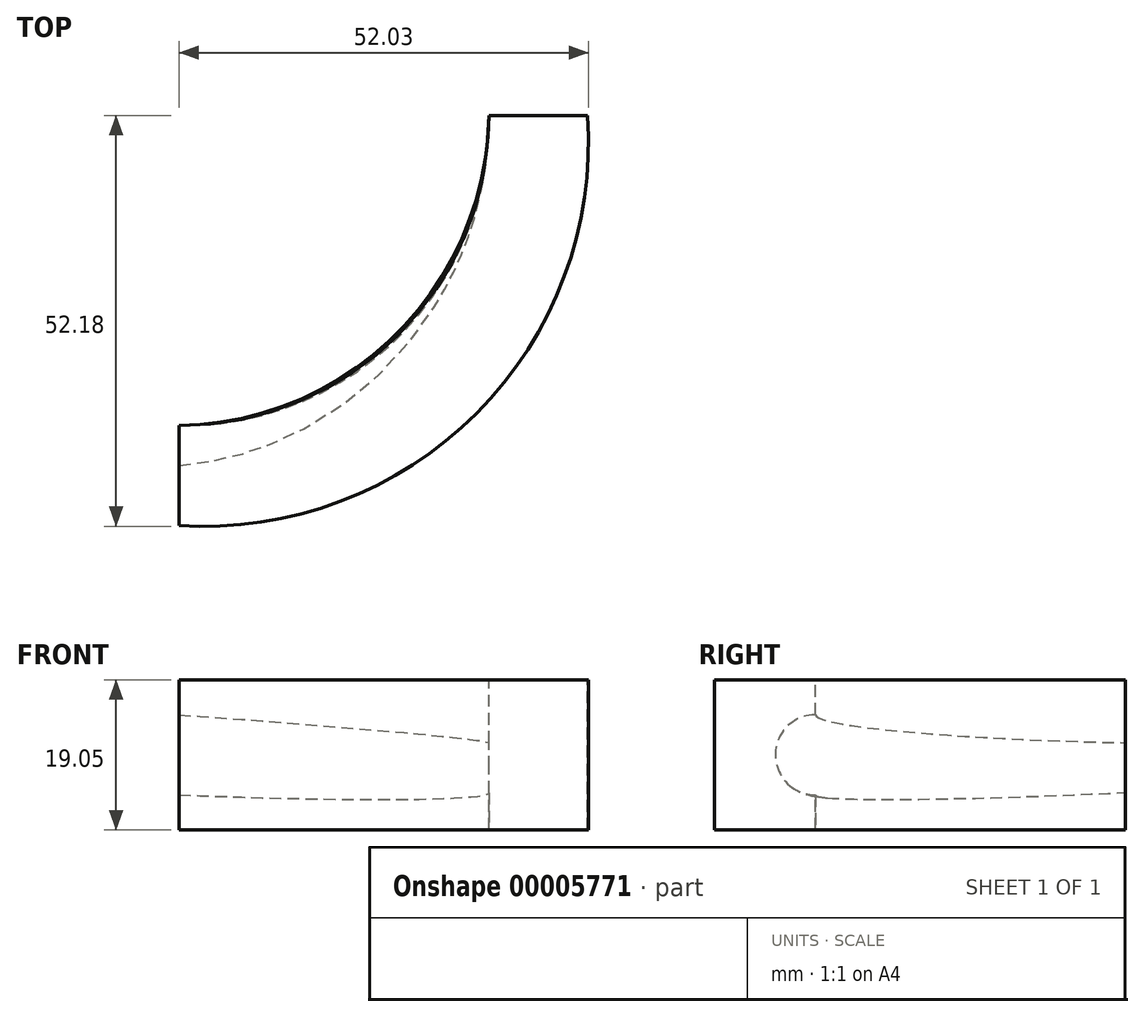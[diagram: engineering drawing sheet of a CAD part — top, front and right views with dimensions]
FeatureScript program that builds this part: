
annotation { "Feature Type Name" : "Feature", "Feature Type Description" : "" }
export const myFeature = defineFeature(function(context is Context, id is Id, definition is map)
    precondition{}
    {
        {
            var Q0;
            Q0=qCreatedBy(makeId("Top.planeOp"),FACE);
            var sketch = newSketch(context, id + "F0", { "sketchPlane" : qUnion([Q0])});
            skLineSegment(sketch, "E0", {"start": v(-39.37, 0) * mm, "end": v(39.37, 0) * mm, "construction": true});
            skLineSegment(sketch, "E1", {"start": v(0, -39.37) * mm, "end": v(0, 39.37) * mm, "construction": true});
            skArc(sketch, "E2", {"start": v(0, -39.37) * mm, "mid": v(27.84, -27.84) * mm, "end": v(39.37, 0) * mm});
            skArc(sketch, "E3", {"start": v(-39.37, 0) * mm, "mid": v(-27.84, -27.84) * mm, "end": v(0, -39.37) * mm});
            skArc(sketch, "E4", {"start": v(0, 39.37) * mm, "mid": v(-27.84, 27.84) * mm, "end": v(-39.37, 0) * mm});
            skArc(sketch, "E5", {"start": v(39.37, 0) * mm, "mid": v(27.84, 27.84) * mm, "end": v(0, 39.37) * mm});
            skSolve(sketch);
        }
        {
            var Q0;
            Q0=qCreatedBy(makeId("Front.planeOp"),FACE);
            var sketch = newSketch(context, id + "F1", { "sketchPlane" : qUnion([Q0])});
            skLineSegment(sketch, "E6", {"start": v(0, -76.2) * mm, "end": v(0, 76.2) * mm, "construction": true});
            skPoint(sketch, "E7", {"position": v(0, 13.82) * mm});
            skPoint(sketch, "E8", {"position": v(0, 6.31) * mm});
            skSolve(sketch);
        }
        {
            var Q0;
            Q0=qCreatedBy(makeId("Right.planeOp"),FACE);
            var sketch = newSketch(context, id + "F2", { "sketchPlane" : qUnion([Q0])});
            skLineSegment(sketch, "E9.0", {"start": v(-39.37, 0) * mm, "end": v(39.37, 0) * mm, "construction": true});
            skLineSegment(sketch, "E10.bottom", {"start": v(39.37, 0) * mm, "end": v(45.72, 0) * mm});
            skLineSegment(sketch, "E10.top", {"start": v(39.37, 19.05) * mm, "end": v(45.72, 19.05) * mm});
            skLineSegment(sketch, "E10.left", {"start": v(39.37, 0) * mm, "end": v(39.37, 19.05) * mm});
            skLineSegment(sketch, "E10.right", {"start": v(45.72, 0) * mm, "end": v(45.72, 19.05) * mm});
            skLineSegment(sketch, "E11.bottom", {"start": v(-39.37, 0) * mm, "end": v(-52.07, 0) * mm});
            skLineSegment(sketch, "E11.top", {"start": v(-39.37, 19.05) * mm, "end": v(-52.07, 19.05) * mm});
            skLineSegment(sketch, "E11.left", {"start": v(-39.37, 0) * mm, "end": v(-39.37, 4.45) * mm});
            skLineSegment(sketch, "E11.right", {"start": v(-52.07, 0) * mm, "end": v(-52.07, 19.05) * mm});
            skArc(sketch, "E12", {"start": v(-39.37, 14.6) * mm, "mid": v(-44.45, 9.52) * mm, "end": v(-39.37, 4.44) * mm});
            skLineSegment(sketch, "E13.trimOffspring", {"start": v(-39.37, 14.6) * mm, "end": v(-39.37, 19.05) * mm});
            skLineSegment(sketch, "E14", {"start": v(-39.37, 14.6) * mm, "end": v(-39.37, 4.45) * mm, "construction": true});
            skLineSegment(sketch, "E15", {"start": v(-39.37, 9.53) * mm, "end": v(-52.07, 9.52) * mm, "construction": true});
            skLineSegment(sketch, "E16", {"start": v(-42.33, 14.6) * mm, "end": v(-39.37, 14.6) * mm, "construction": true});
            skSolve(sketch);
        }
        {
            var Q0;
            Q0=qCreatedBy(makeId("Front.planeOp"),FACE);
            var sketch = newSketch(context, id + "F3", { "sketchPlane" : qUnion([Q0])});
            skLineSegment(sketch, "E17.bottom", {"start": v(-39.37, 0) * mm, "end": v(-53.86, 0) * mm});
            skLineSegment(sketch, "E17.top", {"start": v(-39.37, 19.05) * mm, "end": v(-53.86, 19.05) * mm});
            skLineSegment(sketch, "E17.left", {"start": v(-39.37, 0) * mm, "end": v(-39.37, 19.05) * mm});
            skLineSegment(sketch, "E17.right", {"start": v(-53.86, 0) * mm, "end": v(-53.86, 19.05) * mm});
            skLineSegment(sketch, "E18.bottom", {"start": v(39.37, 0) * mm, "end": v(51.91, 0) * mm});
            skLineSegment(sketch, "E18.top", {"start": v(39.37, 19.05) * mm, "end": v(51.91, 19.05) * mm});
            skLineSegment(sketch, "E18.left", {"start": v(39.37, 0) * mm, "end": v(39.37, 4.74) * mm});
            skLineSegment(sketch, "E18.right", {"start": v(51.91, 0) * mm, "end": v(51.91, 19.05) * mm});
            skLineSegment(sketch, "E19", {"start": v(39.37, 11.06) * mm, "end": v(39.37, 19.05) * mm});
            skLineSegment(sketch, "E20", {"start": v(39.37, 4.74) * mm, "end": v(39.37, 11.06) * mm});
            skSolve(sketch);
        }
        {
            var Q0;
            Q0=qCreatedBy(makeId("Top.planeOp"),FACE);
            var sketch = newSketch(context, id + "F4", { "sketchPlane" : qUnion([Q0])});
            skPoint(sketch, "E21.0", {"position": v(0, 45.72) * mm});
            skPoint(sketch, "E22.0", {"position": v(51.91, 0) * mm});
            skArc(sketch, "E23", {"start": v(51.91, 0) * mm, "mid": v(35.35, 33.53) * mm, "end": v(0, 45.72) * mm});
            skPoint(sketch, "E24.0", {"position": v(0, -52.07) * mm});
            skArc(sketch, "E25", {"start": v(0, -52.07) * mm, "mid": v(37.78, -37.83) * mm, "end": v(51.91, 0) * mm});
            skSolve(sketch);
        }
        {
            var Q0;
            Q0=sQuery(id+"F3.wireOp",VERTEX,"E19.end");
            var Q1;
            Q1=sQuery(id+"F2.wireOp",VERTEX,"E11.right.end");
            var Q2;
            Q2=sQuery(id+"F2.wireOp",VERTEX,"E11.top.start");
            cPlane(context, id + "F5", {"entities" : qUnion([Q0, Q1, Q2]), "cplaneType" : CPlaneType.THREE_POINT, "offset" : 152.4 * mm, "width" : 152.4 * mm, "height" : 152.4 * mm});
        }
        {
            var Q0;
            Q0=qCreatedBy(id+"F5.planeOp",FACE);
            var sketch = newSketch(context, id + "F6", { "sketchPlane" : qUnion([Q0])});
            skArc(sketch, "E26.0", {"start": v(0, -39.37) * mm, "mid": v(27.84, -27.84) * mm, "end": v(39.37, 0) * mm});
            skArc(sketch, "E27.0", {"start": v(0, -52.07) * mm, "mid": v(37.78, -37.83) * mm, "end": v(51.91, 0) * mm});
            skSolve(sketch);
        }
        {
            var Q0;
            Q0=sQuery(id+"F3.wireOp",VERTEX,"E20.end");
            var Q1;
            Q1=sQuery(id+"F2.wireOp",VERTEX,"E13.trimOffspring.start");
            var Q2;
            Q2=sQuery(id+"F1.wireOp",VERTEX,"E7");
            cPlane(context, id + "F7", {"entities" : qUnion([Q0, Q1, Q2]), "cplaneType" : CPlaneType.THREE_POINT, "offset" : 152.4 * mm, "width" : 152.4 * mm, "height" : 152.4 * mm});
        }
        {
            var Q0;
            Q0=sQuery(id+"F1.wireOp",VERTEX,"E8");
            var Q1;
            Q1=sQuery(id+"F3.wireOp",VERTEX,"E18.left.end");
            var Q2;
            Q2=sQuery(id+"F2.wireOp",VERTEX,"E12.end");
            cPlane(context, id + "F8", {"entities" : qUnion([Q0, Q1, Q2]), "cplaneType" : CPlaneType.THREE_POINT, "offset" : 152.4 * mm, "width" : 152.4 * mm, "height" : 152.4 * mm});
        }
        {
            var Q0;
            Q0=qCreatedBy(id+"F7.planeOp",FACE);
            var sketch = newSketch(context, id + "F9", { "sketchPlane" : qUnion([Q0])});
            skPoint(sketch, "E28.0", {"position": v(38.5, -0.22) * mm});
            skPoint(sketch, "E29.0", {"position": v(-0.96, -39.65) * mm});
            skFitSpline(sketch, "E30.0", {"points": [v(-12.2, 37.46) * mm, v(1000, -87.68) * mm, v(15.78, 333.33) * mm, v(-65.94, -59.9) * mm, v(333.33, 9.54) * mm, v(-38.22, 1000) * mm, v(85.02, -16.54) * mm], "construction": true});
            skArc(sketch, "E31", {"start": v(-0.96, -39.65) * mm, "mid": v(26.76, -27.93) * mm, "end": v(38.5, -0.22) * mm});
            skPoint(sketch, "E32", {"position": v(26.76, -27.93) * mm});
            skSolve(sketch);
        }
        {
            var Q0;
            Q0=qCreatedBy(id+"F8.planeOp",FACE);
            var sketch = newSketch(context, id + "F10", { "sketchPlane" : qUnion([Q0])});
            skFitSpline(sketch, "E33.0", {"points": [v(30.18, 25.29) * mm, v(1000, -20.3) * mm, v(85.52, 333.33) * mm, v(-80.65, 34.95) * mm, v(333.33, -30.18) * mm, v(-25.29, 1000) * mm, v(20.3, -85.52) * mm], "construction": true});
            skPoint(sketch, "E34.0", {"position": v(39.15, 0.22) * mm});
            skPoint(sketch, "E35.0", {"position": v(-0.25, -39.11) * mm});
            skArc(sketch, "E36", {"start": v(-0.25, -39.11) * mm, "mid": v(27.78, -27.8) * mm, "end": v(39.15, 0.22) * mm});
            skPoint(sketch, "E37", {"position": v(27.78, -27.8) * mm});
            skSolve(sketch);
        }
        {
            var Q0;
            Q0=makeQuery(id+"F3.imprint","IMPRINT",FACE,{"disambiguationData":[TD([[makeQuery(id+"F3.imprint","IMPRINT",EDGE,{"derivedFrom":sQuery(id+"F3.wireOp",EDGE,"E18.bottom")}),1.0]])]});
            var Q1;
            Q1=makeQuery(id+"F2.imprint","IMPRINT",FACE,{"disambiguationData":[TD([[makeQuery(id+"F2.imprint","IMPRINT",EDGE,{"derivedFrom":sQuery(id+"F2.wireOp",EDGE,"E11.bottom")}),-1.0]])]});
            var Q2;
            Q2=sQuery(id+"F6.wireOp",EDGE,"E27.0");
            var Q3;
            Q3=sQuery(id+"F4.wireOp",EDGE,"E25");
            var Q4;
            Q4=sQuery(id+"F0.wireOp",EDGE,"E2");
            var Q5;
            Q5=sQuery(id+"F6.wireOp",EDGE,"E26.0");
            var Q6;
            Q6=sQuery(id+"F9.wireOp",EDGE,"E31");
            var Q7;
            Q7=sQuery(id+"F10.wireOp",EDGE,"E36");
            loft(context, id + "F11", {"addGuides" : true, "sheetProfilesArray" : [{ "sheetProfileEntities" : qUnion([Q0]) }, { "sheetProfileEntities" : qUnion([Q1]) }], "guidesArray" : [{ "guideEntities" : qUnion([Q2]), "guideDerivativeType" : LoftGuideDerivativeType.DEFAULT, "guideDerivativeMagnitude" : 1 }, { "guideEntities" : qUnion([Q3]), "guideDerivativeType" : LoftGuideDerivativeType.DEFAULT, "guideDerivativeMagnitude" : 1 }, { "guideEntities" : qUnion([Q4]), "guideDerivativeType" : LoftGuideDerivativeType.DEFAULT, "guideDerivativeMagnitude" : 1 }, { "guideEntities" : qUnion([Q5]), "guideDerivativeType" : LoftGuideDerivativeType.DEFAULT, "guideDerivativeMagnitude" : 1 }, { "guideEntities" : qUnion([Q6]), "guideDerivativeType" : LoftGuideDerivativeType.DEFAULT, "guideDerivativeMagnitude" : 1 }, { "guideEntities" : qUnion([Q7]), "guideDerivativeType" : LoftGuideDerivativeType.DEFAULT, "guideDerivativeMagnitude" : 1 }]});
        }
    });
